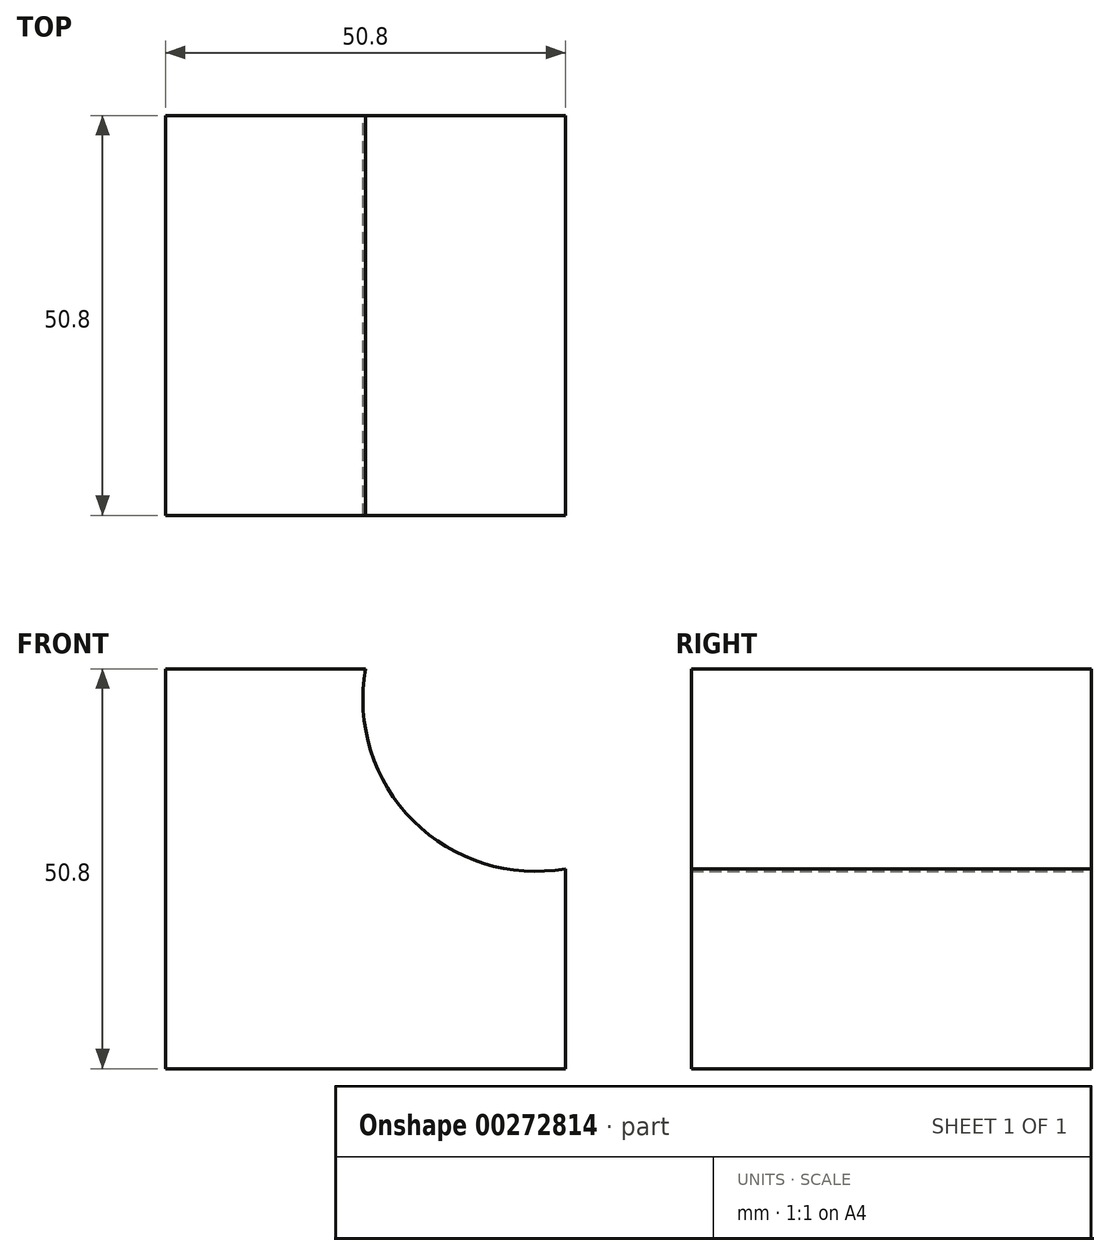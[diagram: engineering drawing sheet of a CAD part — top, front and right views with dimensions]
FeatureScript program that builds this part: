
annotation { "Feature Type Name" : "Feature", "Feature Type Description" : "" }
export const myFeature = defineFeature(function(context is Context, id is Id, definition is map)
    precondition{}
    {
        {
            var Q0;
            Q0=qCreatedBy(makeId("Front.planeOp"),FACE);
            var sketch = newSketch(context, id + "F0", { "sketchPlane" : qUnion([Q0])});
            skLineSegment(sketch, "E0", {"start": v(0, 0) * mm, "end": v(-50.8, 0) * mm});
            skLineSegment(sketch, "E1", {"start": v(-50.8, 0) * mm, "end": v(-50.8, 50.8) * mm});
            skLineSegment(sketch, "E2", {"start": v(-50.8, 50.8) * mm, "end": v(-25.4, 50.8) * mm});
            skLineSegment(sketch, "E3", {"start": v(0, 25.4) * mm, "end": v(0, 0) * mm});
            skArc(sketch, "E4", {"start": v(-25.4, 50.8) * mm, "mid": v(-19.33, 31.47) * mm, "end": v(0, 25.4) * mm});
            skSolve(sketch);
        }
        {
            var Q0;
            Q0=makeQuery(id+"F0.imprint","IMPRINT",FACE,{"disambiguationData":[TD([[makeQuery(id+"F0.imprint","IMPRINT",EDGE,{"derivedFrom":sQuery(id+"F0.wireOp",EDGE,"E0")}),-1.0]])]});
            extrude(context, id + "F1", {"entities" : qUnion([Q0]), "depth" : 50.8 * mm});
        }
    });
